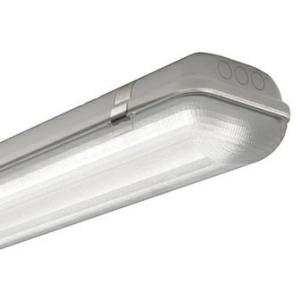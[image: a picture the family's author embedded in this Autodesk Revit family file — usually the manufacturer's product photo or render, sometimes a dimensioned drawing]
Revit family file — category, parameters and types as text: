
# Revit family: 3f_filippi_-_3f_linda_3f_filippi_-_58626_-_3f_linda_led_2x22w_ep_l1570
name_source: partatom
category: Lighting Fixtures
units: mm (PartAtom-declared; Revit-internal decimal feet)

## family parameters
Cut with Voids When Loaded = No
Host = Face
Light Source = No
Part Type = Normal
Room Calculation Point = No
Round Connector Dimension = Use Diameter
Shared = No

## types (1)
- 3F Filippi - 3F Linda (1 x LED, 7557 lm, 50 W, 4000 K)
    Apparent Load = 50 VA
    Approval mark = ENEC
    CIE Flux Codes = 46 76 93 97 100
    Color Rendering = 80
    Color Temperature = 4000 K
    Control Gear = Electronic ballast
    Default Elevation = 1800 mm
    Description = ILLUMINOTECHNICAL
Luminous efficiency 100% (DLOR 97%, ULOR 3%).
Initial luminous flux of the luminaire 7557 lm.
Emergency luminaire luminous flux BLF 7.6%.
Controlled symmetric distribution.
Installation Interdistance Transv.D = 1.52 x hu - Long.D = 1.17 x hu.
Tabular UGR (CIE 117 - 4H-8H; S=0.25H; 70/50/20): RUG 23.5 - 22.7.
Beam angle: 94° - 78°.
Luminous efficacy 151 lm/W.
Lifetime (L93/B10): 30000 h. (tq+25°C)
Lifetime (L90/B10): 50000 h. (tq+25°C)
Lifetime (L85/B10): 80000 h. (tq+25°C)
Lifetime (L80/B10): 100000 h. (tq+25°C)
Sudden decreased luminous flux after 50000 hours: 0% (C0).
Photobiological safety in compliance with IEC/TR 62778: RG0 risk exempt, (IEC 62471).
In compliance with IEC/EN 62722-2-1 - IEC/EN 62717 standards.

SOURCE
2 linear LED modules 22W/840.
Energy efficiency class (UE 2019/2020 - UE 2019/2015): D.
CIE 13.3 Colour rendering index: CRI >80 (R9 <50%).
IES TM-30 Fidelity Index: Rf = 84 Rg = 95.
CCT nominal colour temperature 4000 K.
Colour initial tolerance (MacAdam): SDCM 3.

MECHANICAL
Self-extinguishing V2 polycarbonate housing, injection moulded, RAL 7035 grey.
Ecologic anti-aging injected sealing gasket.
Diffuser in self-extinguishing V2 polycarbonate, photo-engraved interior, UV stabilised, injection moulded with smooth outer surface, tamper-proof opening.
Gear-holder reflector in hot-dip galvanised steel, painted with white polyester base.
Snug fit safety snap-lock clips for diffuser mounting in stainless steel, screwdriver opening.
Fixing brackets in stainless steel.
Possibility for technicians to access the interior of the luminaire.
Luminaire with limited surface temperature. - D - (EN 60598-2-24)
Dimensions: 1570x160 mm, height 100 mm. Weight 3.845 kg.
IP66 protection degree.
Mechanical strength to impacts IK10 (20 joule).
Glow-wire test resistance 850°C.

ELECTRICAL
Halogen Free electronic wiring 230V-50/60Hz, power factor 0.90, THD <25%, constant output current, SELV, class I, 1 driver.
Power of the luminaire 50 W.
CE - IEC 60598-1 - EN 60598-1.
EP maintained emergency wiring on board, 1h duration, 24h recharge; compliant with EN 60598-2-22, excluding high risk areas.
SAFE FLICKER: PstLM=<1 and SVM=<0.4 (IEC TR 61547-1 and IEC TR 63158), to ensure a more comfortable and safe light.
Ambient temperature from +5°C to +25°C.
Temperature class T6 max 85°C.
Relative humidity UR: <85%.

INSTALLATION
Ceiling / Suspended / Wall.
All accessories dedicated to this product are available on the Catalog and on our website www.3F-Filippi.com.

APPLICATIONS
Suitable product for food production plants (HACCP), IFS (Food Version 6), BRC (GSFS Food Version 7).
Dry, dusty indoor environments, subject to occasional water splashes.
Virtually shatterproof polycarbonate compatibly with the fumes / atmospheres that compromise the elasticity of plastic materials.
Not suitable for installation on surfaces subject to important vibrations, exposed to weather conditions, on ropes or poles.
Suitable for illumination of public car parks and parking grounds referred to DIN 67528:2018-04.

WARNING
Fixture not suitable for cold stores with an ambient temperature <5°C and/or relative humidity >85%.
Luminaire designed for disposal/recycling at end-of-life.
Replaceable (LED only) light source by a professional. Replaceable control gear by a professional.
    Height = 100 mm  [stored 0.328084 ft]
    Lamp = 1 x LED
    Lamp Light Flux = 7557 lm
    Lamp Power = 50 W
    Lamp count = 1
    Length = 1570 mm
    Lifetime = 50000 h
    Luminous efficacy = 151 lm/W
    Manufacturer = 3F Filippi
    ModVariant = No
    Model = 3F Filippi - 58626 - 3F Linda LED 2x22W EP L1570
    Mounting Place = Ceiling
    Mounting Type = Pendant
    Number of Poles = 1
    OnlyDefault = Yes
    Power Factor = 1
    Product Name = 3F Filippi - 3F Linda
    Product group = pendant luminaire
    ProductGroupID = 9
    Protection Class = Protection class I
    Protection Degree = IP 66
    RLX_Detail_Level = 1
    RLX_Emergency_Light_Flux = 0 lm
    RLX_Emergency_Type = 0
    RLX_Emergency_Type_DB = No
    RlxData = <blob elided: 71405 chars, md5=829bd2e5>
    Socket = socket
    Standby Power = 0 W
    System Light Flux = 7557 lm
    System Power = 50 W
    Type Comments = Product without accessories
    Type Image = 3ffilippi_3f_linda_led_2x.jpg
    URL = http://relux.com
    VarID = ---
    Voltage = 0 V
    Weight = 0.00 kg
    Width = 160 mm

note: [stored X ft] marks values corroborated as IEEE doubles in the binary element streams (Revit-internal decimal feet)

## geometry (parser evidence)
native form markers: Blend x4, Sweep x9
no freeform markers — native parametric forms only
